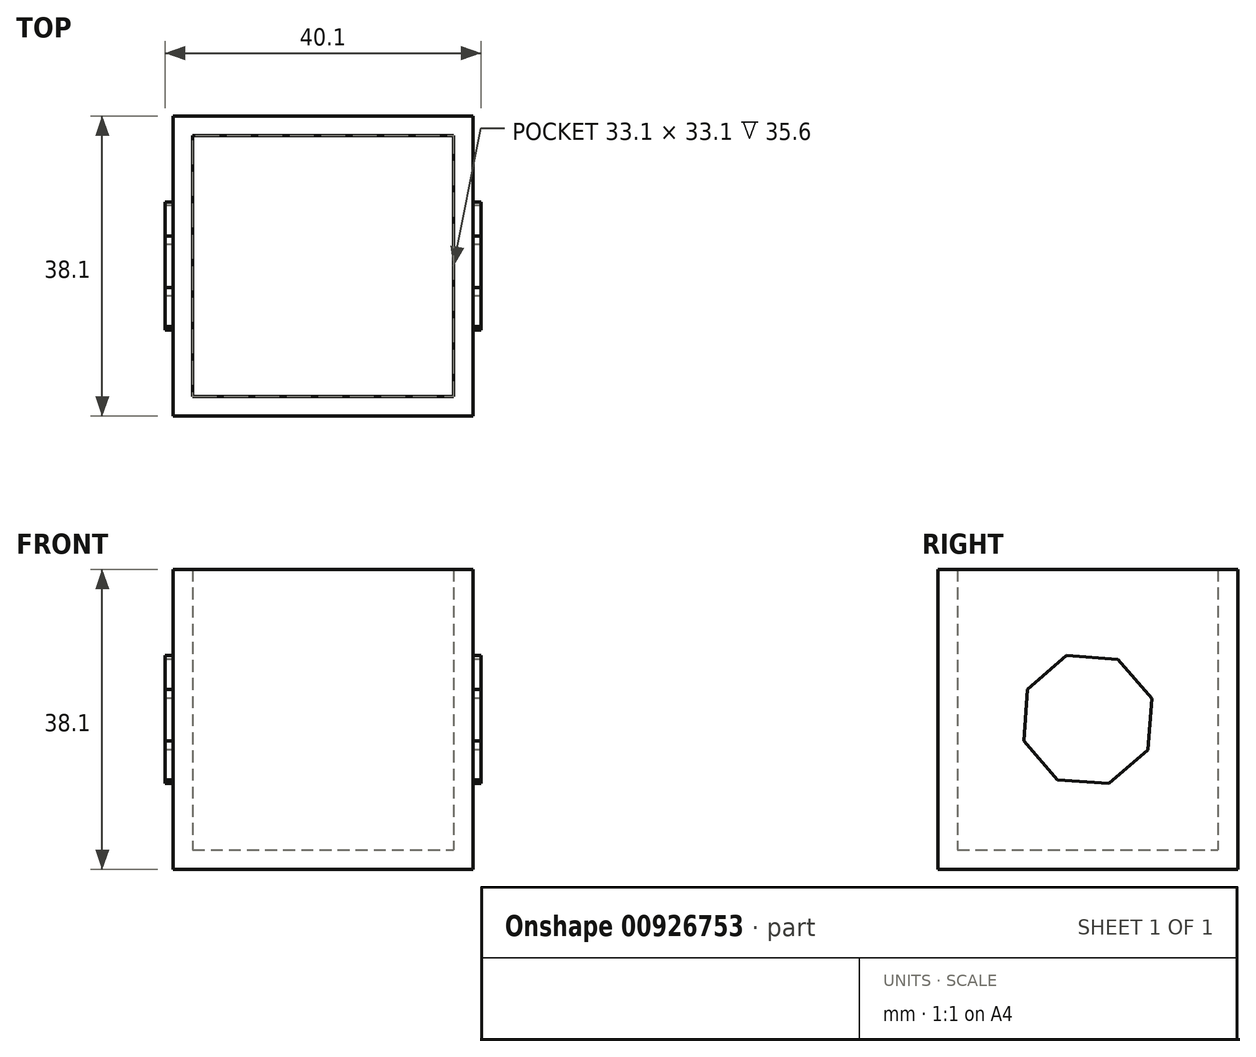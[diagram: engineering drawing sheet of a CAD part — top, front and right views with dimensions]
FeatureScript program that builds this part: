
annotation { "Feature Type Name" : "Feature", "Feature Type Description" : "" }
export const myFeature = defineFeature(function(context is Context, id is Id, definition is map)
    precondition{}
    {
        {
            var Q0;
            Q0=qCreatedBy(makeId("Top.planeOp"),FACE);
            var sketch = newSketch(context, id + "F0", { "sketchPlane" : qUnion([Q0])});
            skLineSegment(sketch, "E0.bottom", {"start": v(0, 0) * mm, "end": v(38.1, 0) * mm});
            skLineSegment(sketch, "E0.top", {"start": v(0, 38.1) * mm, "end": v(38.1, 38.1) * mm});
            skLineSegment(sketch, "E0.left", {"start": v(0, 0) * mm, "end": v(0, 38.1) * mm});
            skLineSegment(sketch, "E0.right", {"start": v(38.1, 0) * mm, "end": v(38.1, 38.1) * mm});
            skSolve(sketch);
        }
        {
            var Q0;
            Q0=makeQuery(id+"F0.imprint","IMPRINT",FACE,{"disambiguationData":[TD([[makeQuery(id+"F0.imprint","IMPRINT",EDGE,{"derivedFrom":sQuery(id+"F0.wireOp",EDGE,"E0.bottom")}),1.0]])]});
            extrude(context, id + "F1", {"entities" : qUnion([Q0]), "depth" : 38.1 * mm, "offsetDistance" : 25 * mm});
        }
        {
            var Q0;
            Q0=makeQuery(id+"F1.opExtrude","CAP_FACE",FACE,{"disambiguationData":[OSD([sQuery(id+"F0.wireOp",EDGE,"E0.bottom"),sQuery(id+"F0.wireOp",EDGE,"E0.top"),sQuery(id+"F0.wireOp",EDGE,"E0.left"),sQuery(id+"F0.wireOp",EDGE,"E0.right")])],"isStart":false});
            shell(context, id + "F2", {"entities" : qUnion([Q0]), "thickness" : 2.5 * mm});
        }
        {
            var Q0;
            Q0=makeQuery(id+"F1.opExtrude","SWEPT_FACE",FACE,{"disambiguationData":[OSD([sQuery(id+"F0.wireOp",EDGE,"E0.right")])]});
            var sketch = newSketch(context, id + "F3", { "sketchPlane" : qUnion([Q0])});
            skCircle(sketch, "E1.cCircle", {"center": v(19.05, 19.05) * mm, "radius": 7.91 * mm, "construction": true});
            skLineSegment(sketch, "E1.0", {"start": v(10.92, 16.35) * mm, "end": v(15.21, 11.4) * mm});
            skLineSegment(sketch, "E1.1", {"start": v(11.4, 22.89) * mm, "end": v(10.92, 16.35) * mm});
            skLineSegment(sketch, "E1.2", {"start": v(16.35, 27.18) * mm, "end": v(11.4, 22.89) * mm});
            skLineSegment(sketch, "E1.3", {"start": v(22.89, 26.7) * mm, "end": v(16.35, 27.18) * mm});
            skLineSegment(sketch, "E1.4", {"start": v(27.18, 21.75) * mm, "end": v(22.89, 26.7) * mm});
            skLineSegment(sketch, "E1.5", {"start": v(26.7, 15.21) * mm, "end": v(27.18, 21.75) * mm});
            skLineSegment(sketch, "E1.6", {"start": v(21.75, 10.92) * mm, "end": v(26.7, 15.21) * mm});
            skLineSegment(sketch, "E1.7", {"start": v(15.21, 11.4) * mm, "end": v(21.75, 10.92) * mm});
            skPoint(sketch, "E1.0.midPoint", {"position": v(13.07, 13.87) * mm});
            skSolve(sketch);
        }
        {
            var Q0;
            Q0=makeQuery(id+"F3.imprint","IMPRINT",FACE,{"disambiguationData":[TD([[makeQuery(id+"F3.imprint","IMPRINT",EDGE,{"derivedFrom":sQuery(id+"F3.wireOp",EDGE,"E1.0")}),1.0]])]});
            extrude(context, id + "F4", {"entities" : qUnion([Q0]), "depth" : 1 * mm, "offsetDistance" : 25 * mm});
        }
        {
            var Q0;
            Q0=makeQuery(id+"F4.opExtrude","SWEPT_BODY",BODY,{"disambiguationData":[OSD([sQuery(id+"F3.wireOp",EDGE,"E1.0"),sQuery(id+"F3.wireOp",EDGE,"E1.1"),sQuery(id+"F3.wireOp",EDGE,"E1.2"),sQuery(id+"F3.wireOp",EDGE,"E1.3"),sQuery(id+"F3.wireOp",EDGE,"E1.4"),sQuery(id+"F3.wireOp",EDGE,"E1.5"),sQuery(id+"F3.wireOp",EDGE,"E1.6"),sQuery(id+"F3.wireOp",EDGE,"E1.7")])]});
            transform(context, id + "F5", {"entities" : qUnion([Q0]), "transformType" : TransformType.TRANSLATION_3D, "dx" : -39.1 * mm, "dy" : 0 * mm, "dz" : 0 * mm, "makeCopy" : true});
        }
    });
